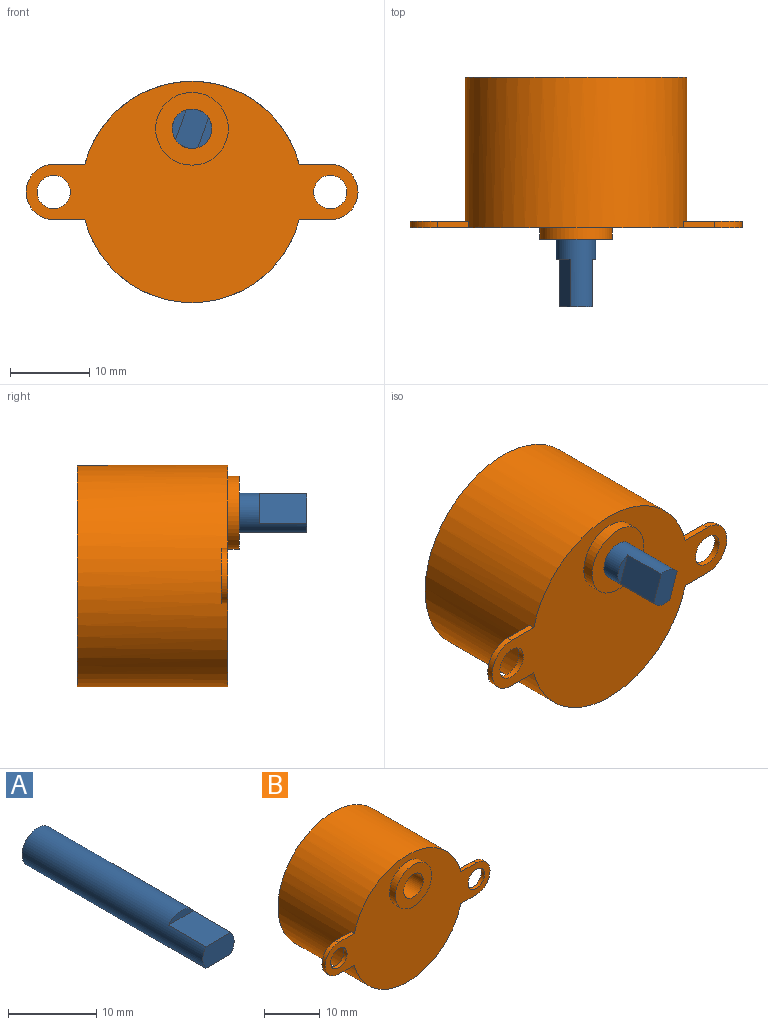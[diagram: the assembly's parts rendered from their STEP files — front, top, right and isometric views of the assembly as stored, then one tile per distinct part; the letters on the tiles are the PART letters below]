
ASSEMBLY  parts=2 mates=1
PART A: 7 faces, bbox 5x29x5 mm
  f0: plane 5x3mm, normal (0,-1,0), area 14mm2, adj f1,f3,f5
  f1: cylinder r=2.5mm len=29mm, axis (0,1,0), area 399.9mm2, adj f0,f2,f3,f4,f5,f6
  f2: plane 5x5mm, normal (0,1,0), area 19.6mm2, adj f1
  f3: plane 6x4mm, normal (0,0,-1), area 24mm2, adj f0,f1,f4
  f4: plane 4x1mm, normal (0,-1,0), area 2.8mm2, adj f1,f3
  f5: plane 6x4mm, normal (0,0,1), area 24mm2, adj f0,f1,f6
  f6: plane 4x1mm, normal (0,-1,0), area 2.8mm2, adj f1,f5
PART B: 16 faces, bbox 42x20.5x28 mm
  f0: cylinder r=14mm len=28mm, axis (0,-1,0), area 1660mm2, adj f2,f3,f4,f5,f8,f9,f12,f13
  f1: cylinder r=2.5mm len=20.5mm, axis (0,-1,0), area 322mm2, adj f2,f15
  f2: plane 28x28mm, normal (0,1,0), area 596.1mm2, adj f0,f1
  f3: plane 42x28mm, normal (0,-1,0), area 611.1mm2, adj f0,f4,f5,f6,f7,f9,f10,f11
  f4: plane 3.94x0.8mm, normal (0,0,1), area 3.2mm2, adj f0,f3,f6,f8
  f5: plane 3.94x0.8mm, normal (0,0,-1), area 3.2mm2, adj f0,f3,f6,f8
  f6: cylinder r=3.5mm len=7mm, axis (0,-1,0), area 8.8mm2, adj f3,f4,f5,f8
  f7: cylinder r=2.1mm len=4.2mm, axis (0,-1,0), area 10.6mm2, adj f3,f8
  f8: plane 7.44x7mm, normal (0,1,0), area 30.9mm2, adj f0,f4,f5,f6,f7
  f9: plane 3.94x0.8mm, normal (0,0,1), area 3.2mm2, adj f0,f3,f10,f13
  f10: cylinder r=3.5mm len=7mm, axis (0,-1,0), area 8.8mm2, adj f3,f9,f12,f13
  f11: cylinder r=2.1mm len=4.2mm, axis (0,-1,0), area 10.6mm2, adj f3,f13
  f12: plane 3.94x0.8mm, normal (0,0,-1), area 3.2mm2, adj f0,f3,f10,f13
  f13: plane 7.44x7mm, normal (0,1,0), area 30.9mm2, adj f0,f9,f10,f11,f12
  f14: cylinder r=4.6mm len=9.2mm, axis (0,1,0), area 43.4mm2, adj f3,f15
  f15: plane 9.2x9.2mm, normal (0,-1,0), area 46.8mm2, adj f1,f14
PLACE A rot(axis=(0,1,0),109.6deg) t=(0,0,0)mm
PLACE B at identity fixed
MATE revolute A.f1 <-> B.f1  axis (0,1,0) through (0,19,0)mm
